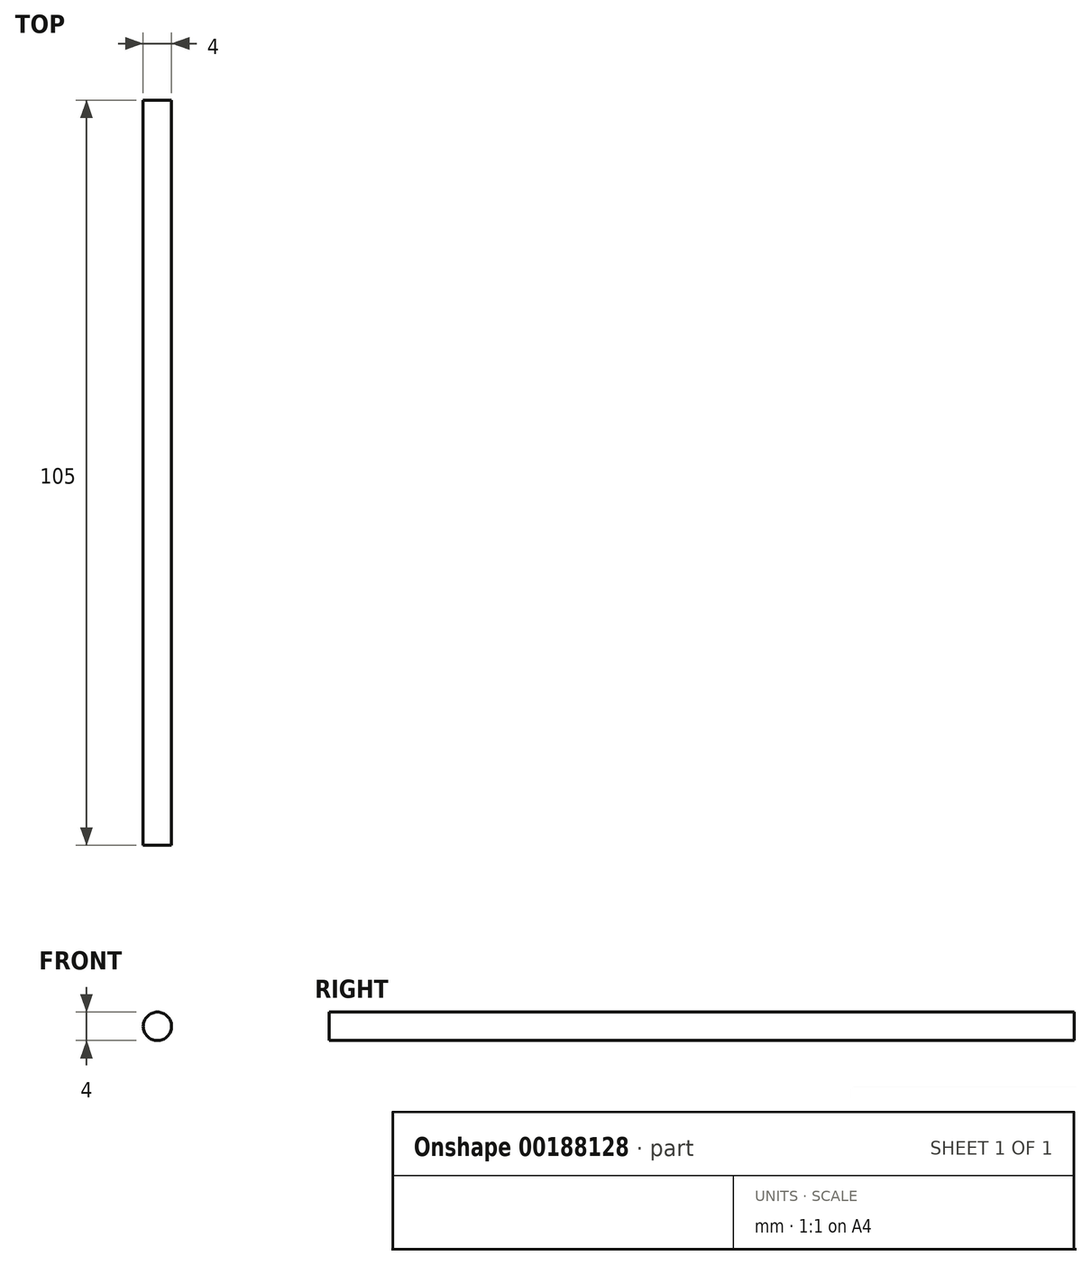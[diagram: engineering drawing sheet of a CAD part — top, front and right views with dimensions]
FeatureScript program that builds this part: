
annotation { "Feature Type Name" : "Feature", "Feature Type Description" : "" }
export const myFeature = defineFeature(function(context is Context, id is Id, definition is map)
    precondition{}
    {
        {
            var Q0;
            Q0=qCreatedBy(makeId("Front.planeOp"),FACE);
            var sketch = newSketch(context, id + "F1", { "sketchPlane" : qUnion([Q0])});
            skCircle(sketch, "E0", {"center": v(0, 0) * mm, "radius": 2 * mm});
            skSolve(sketch);
        }
        {
            var Q0;
            Q0=makeQuery(id+"F1.imprint","IMPRINT",FACE,{"disambiguationData":[TD([[makeQuery(id+"F1.imprint","IMPRINT",EDGE,{"derivedFrom":sQuery(id+"F1.wireOp",EDGE,"E0")}),1.0]])]});
            extrude(context, id + "F0", {"entities" : qUnion([Q0]), "depth" : 105 * mm});
        }
    });
